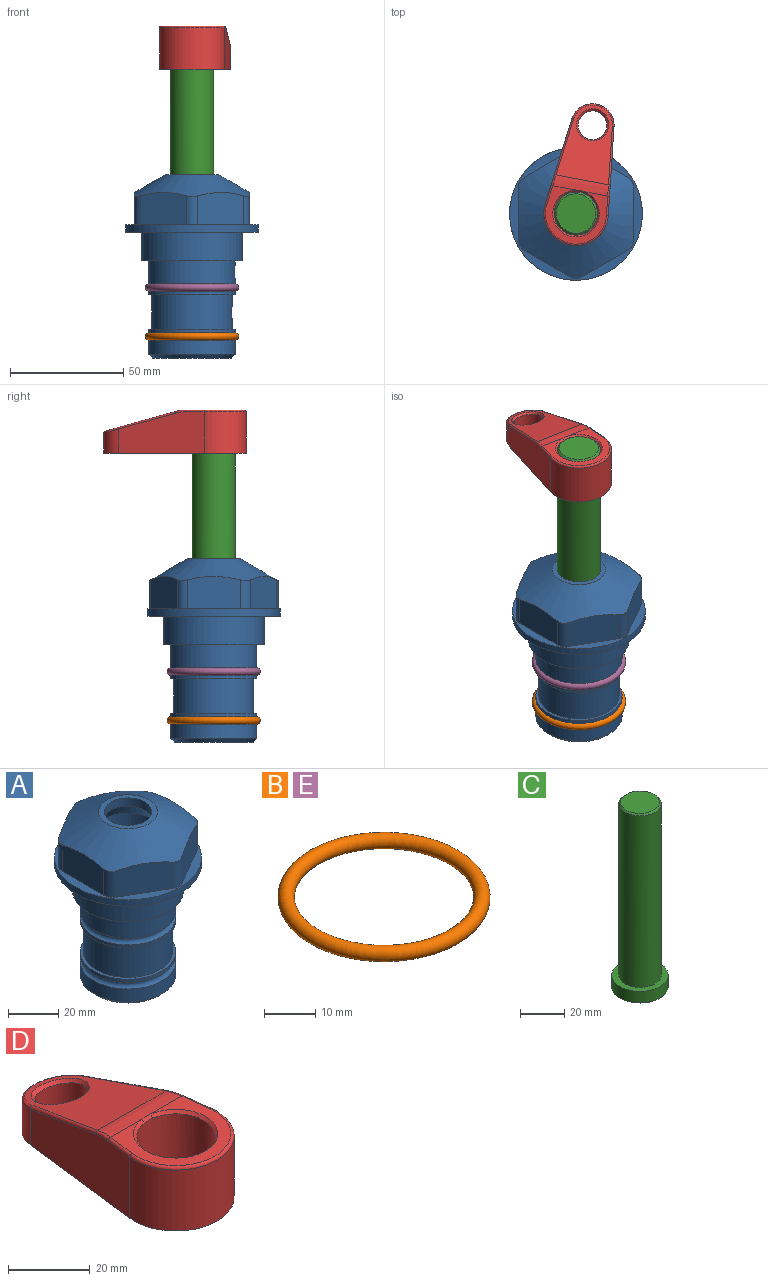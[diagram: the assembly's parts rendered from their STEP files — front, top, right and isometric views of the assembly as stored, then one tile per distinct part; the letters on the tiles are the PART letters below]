
ASSEMBLY  parts=5 mates=4
PART A: 36 faces, bbox 58.7x58.7x81 mm
  f0: cylinder r=17.78mm len=35.56mm, axis (0,0,1), area 1670.8mm2, adj f23,f24,f31
  f1: cylinder r=19.05mm len=38.1mm, axis (0,0,1), area 1191.9mm2, adj f26,f27,f30
  f2: plane 58.66x58.66mm, normal (0,0,-1), area 1150.6mm2, adj f3,f28
  f3: cylinder r=29.33mm len=58.66mm, axis (0,0,-1), area 585.1mm2, adj f2,f4
  f4: plane 58.66x58.66mm, normal (0,0,1), area 475.9mm2, adj f3,f5,f6,f7,f8,f9,f10,f11
  f5: plane 20.32x14.34mm, normal (-0.5,0.87,0), area 324.4mm2, adj f4,f15,f16,f17
  f6: plane 20.32x14.34mm, normal (0.5,0.87,0), area 324.4mm2, adj f4,f14,f15,f17
  f7: plane 23.48x14.34mm, normal (1,0,0), area 324.4mm2, adj f4,f13,f14,f17
  f8: plane 20.32x14.34mm, normal (0.5,-0.87,0), area 324.4mm2, adj f4,f12,f13,f17
  f9: plane 20.32x14.34mm, normal (-0.5,-0.87,0), area 324.4mm2, adj f4,f11,f12,f17
  f10: plane 23.48x14.34mm, normal (-1,0,0), area 324.4mm2, adj f4,f11,f16,f17
  f11: cylinder r=5.08mm len=12.85mm, axis (0,0,-1), area 67.2mm2, adj f4,f9,f10,f17
  f12: cylinder r=5.08mm len=12.85mm, axis (0,0,-1), area 67.2mm2, adj f4,f8,f9,f17
  f13: cylinder r=5.08mm len=12.85mm, axis (0,0,-1), area 67.2mm2, adj f4,f7,f8,f17
  f14: cylinder r=5.08mm len=12.85mm, axis (0,0,-1), area 67.2mm2, adj f4,f6,f7,f17
  f15: cylinder r=5.08mm len=12.85mm, axis (0,0,-1), area 67.2mm2, adj f4,f5,f6,f17
  f16: cylinder r=5.08mm len=12.85mm, axis (0,0,-1), area 67.2mm2, adj f4,f5,f10,f17
  f17: cone r=11.73mm half-angle=60deg, axis (0,0,-1), area 2071.8mm2, adj f5,f6,f7,f8,f9,f10,f11,f12
  f18: plane 23.46x23.46mm, normal (0,0,1), area 147.4mm2, adj f17,f35
  f19: plane 34.93x34.93mm, normal (0,0,-1), area 958mm2, adj f29
  f20: cylinder r=19.05mm len=38.1mm, axis (0,0,1), area 760.1mm2, adj f21,f29
  f21: torus R=19.05mm, axis (0,0,1), area 565.3mm2, adj f20,f22
  f22: cylinder r=19.05mm len=38.1mm, axis (0,0,1), area 190mm2, adj f21,f23
  f23: plane 38.1x38.1mm, normal (0,0,1), area 146.9mm2, adj f0,f22
  f24: plane 38.1x38.1mm, normal (0,0,-1), area 146.9mm2, adj f0,f25
  f25: cylinder r=19.05mm len=38.1mm, axis (0,0,1), area 190mm2, adj f24,f26
  f26: torus R=19.05mm, axis (0,0,1), area 565.3mm2, adj f1,f25
  f27: plane 44.45x44.45mm, normal (0,0,-1), area 411.7mm2, adj f1,f28
  f28: cylinder r=22.23mm len=44.45mm, axis (0,0,1), area 1773.5mm2, adj f2,f27
  f29: cone r=19.05mm half-angle=45deg, axis (0,0,1), area 257.5mm2, adj f19,f20
  f30: cylinder r=3.17mm len=6.75mm, axis (-1,0,0), area 128mm2, adj f1,f33
  f31: cylinder r=3.17mm len=6.35mm, axis (-1,0,0), area 102.5mm2, adj f0,f33
  f32: plane 25.4x25.4mm, normal (0,0,1), area 506.7mm2, adj f33
  f33: cylinder r=12.7mm len=66.42mm, axis (0,0,-1), area 5236.2mm2, adj f30,f31,f32,f34
  f34: cone r=9.53mm half-angle=30deg, axis (0,0,-1), area 443.4mm2, adj f33,f35
  f35: cylinder r=9.53mm len=19.05mm, axis (0,0,-1), area 240.9mm2, adj f18,f34
PART B: 1 faces, bbox 44.7x44.7x3.2 mm
  f0: torus R=19.05mm, axis (0,0,1), area 1193.9mm2
PART C: 6 faces, bbox 25.4x25.4x101.6 mm
  f0: plane 17.46x17.46mm, normal (0,0,1), area 239.5mm2, adj f5
  f1: plane 25.4x25.4mm, normal (0,0,-1), area 506.7mm2, adj f2
  f2: cylinder r=12.7mm len=25.4mm, axis (0,0,1), area 506.7mm2, adj f1,f3
  f3: plane 25.4x25.4mm, normal (0,0,1), area 221.7mm2, adj f2,f4
  f4: cylinder r=9.53mm len=94.46mm, axis (0,0,1), area 5653mm2, adj f3,f5
  f5: cone r=8.73mm half-angle=45deg, axis (0,0,-1), area 64.4mm2, adj f0,f4
PART D: 31 faces, bbox 31.7x65.5x19.8 mm
  f0: plane 39.12x18.26mm, normal (0.99,0.12,0), area 612.2mm2, adj f1,f4,f7,f11,f13,f15
  f1: cylinder r=9.53mm len=18.91mm, axis (0,0,-1), area 296.1mm2, adj f0,f2,f7,f17
  f2: plane 39.12x18.26mm, normal (-0.99,0.12,0), area 612.2mm2, adj f1,f4,f7,f12,f14,f16
  f3: cylinder r=6.35mm len=12.7mm, axis (0,0,-1), area 362.4mm2, adj f7,f18
  f4: cylinder r=14.29mm len=28.58mm, axis (0,0,-1), area 882.2mm2, adj f0,f2,f7,f10
  f5: cylinder r=9.53mm len=19.05mm, axis (0,0,-1), area 1092.6mm2, adj f7,f19,f20
  f6: plane 26.99x23.69mm, normal (0,0,1), area 216.2mm2, adj f9,f10,f11,f12,f19
  f7: plane 63.5x28.58mm, normal (0,0,-1), area 661.8mm2, adj f0,f1,f2,f3,f4,f5,f22,f23
  f8: plane 33.52x23.6mm, normal (0,0.26,0.97), area 486mm2, adj f9,f15,f16,f17,f18
  f9: cylinder r=19.05mm len=24.72mm, axis (1,0,0), area 120.4mm2, adj f6,f8,f13,f14,f20
  f10: torus R=13.49mm, axis (0,0,1), area 59mm2, adj f4,f6,f11,f12
  f11: cylinder r=0.79mm len=8.67mm, axis (0.12,-0.99,0), area 10.8mm2, adj f0,f6,f10,f13
  f12: cylinder r=0.79mm len=8.67mm, axis (0.12,0.99,0), area 10.8mm2, adj f2,f6,f10,f14
  f13: bspline ~4.95x1.42mm, area 6.1mm2, adj f0,f9,f11,f15
  f14: bspline ~4.95x1.42mm, area 6.1mm2, adj f2,f9,f12,f16
  f15: cylinder r=0.79mm len=25.95mm, axis (0.12,-0.96,0.26), area 32.9mm2, adj f0,f8,f13,f17
  f16: cylinder r=0.79mm len=25.95mm, axis (0.12,0.96,-0.26), area 32.9mm2, adj f2,f8,f14,f17
  f17: bspline ~18.91x8.38mm, area 30mm2, adj f1,f8,f15,f16
  f18: bspline ~14.29x14.29mm, area 48.3mm2, adj f3,f8
  f19: cone r=9.53mm half-angle=45deg, axis (0,0,1), area 66.5mm2, adj f5,f6,f20
  f20: bspline ~3.22x0.96mm, area 3.5mm2, adj f5,f9,f19
  f21: plane 2.75x2.72mm, normal (0,0,-1), area 2.9mm2, adj f23,f25,f28
  f22: plane 23.05x15.88mm, normal (-0.99,-0.12,0), area 323.6mm2, adj f7,f25,f26,f27,f28,f29
  f23: plane 23.05x15.88mm, normal (0.99,-0.12,0), area 323.6mm2, adj f7,f21,f25,f27,f28,f30
  f24: cylinder r=9.53mm len=10.69mm, axis (0,0,-1), area 114.7mm2, adj f7,f27,f29,f30
  f25: cylinder r=12.7mm len=20.59mm, axis (0,0,-1), area 381.1mm2, adj f7,f21,f22,f23,f26,f28
  f26: plane 2.75x2.72mm, normal (0,0,-1), area 2.9mm2, adj f22,f25,f28
  f27: plane 19.72x18.37mm, normal (0,-0.26,-0.97), area 291.8mm2, adj f22,f23,f24,f28,f29,f30
  f28: cylinder r=15.88mm len=19.92mm, axis (1,0,0), area 54.8mm2, adj f21,f22,f23,f25,f26,f27
  f29: cylinder r=1.59mm len=11mm, axis (0,0,-1), area 34.7mm2, adj f7,f22,f24,f27
  f30: cylinder r=1.59mm len=11mm, axis (0,0,-1), area 34.7mm2, adj f7,f23,f24,f27
PART E: same geometry as B
PLACE A at identity fixed
PLACE B t=(0,0,-21.59)mm
PLACE C rot(axis=(0,0,-1),10.6deg) t=(0,0,27.55)mm
PLACE D rot(axis=(0,0,-1),10.6deg) t=(0,0,27.55)mm
PLACE E at identity
MATE cylindrical C.f2 <-> A.f0  axis (0,0,-1) through (0,0,-10.55)mm
MATE fastened E.f0 <-> A.f0  axis (0,0,1) through (0,0,-24.51)mm
MATE fastened D.f4 <-> C.f2  axis (0,0,1) through (0,0,91.05)mm
MATE fastened B.f0 <-> A.f0  axis (0,0,1) through (0,0,-46.1)mm
